# Revit family: Water_Boiler-Navien-NFB-C-Condensing-NFB-301C-02
name_source: partatom
category: Mechanical Equipment
revit_build: Autodesk Revit 2017 (Build: 20160225_1515(x64)
units: mm (PartAtom-declared; Revit-internal decimal feet)

## family parameters
Cut with Voids When Loaded = No
Host = Face
OmniClass Number = 23.65.35.11
OmniClass Title = Supply Water Heaters
Part Type = Normal
Room Calculation Point = No
Round Connector Dimension = Use Diameter
Shared = No

## types (1)
- NFB-301C
    Apparent Load = 0 VA
    Assembly Code = D3010500
    Certifications = Energy Star | AHRI | CSA | ASME | CSA Blue Star | CSA Blue Flame
    Condensate Outlet = 0.8 "
    Default Elevation = 48 "
    Depth = 22.3 "
    Description = High Efficiency Condensing Heating Boiler
    Exhaust = 3"
    Finish = Metal - Navien - Stainless Steel
    Frequency = 60 Hz
    Gas Connection Size = 1"
    Heating Capacity = 293000.0 Btu/h
    Heating Capacity Note = 20000 to 301000 BTUh
    Heating Return = 1.3 "
    Heating Supply = 1.3 "
    Height = 32.8 "
    Ignition = Electronic ignition
    Installation Type = Indoor Wall-Hung
    Intake = 3"
    Keynote = 22 33 00.A1
    Manufacturer = Navien, Inc.
    Manufacturer Fax Number = (949) 420-0430
    Model = NFB-301C
    Natural Gas Manifold Pressure = -0.06" to -0.87" WC
    Natural Gas Supply Pressure = 3.5" to 10.5" WC
    Number of Poles = 1
    Optional Heating Return = 1.3 "
    Optional Heating Supply = 1.3 "
    Phase = 1
    Power Factor = 1
    Product Documentation Link = https://www.navieninc.com
    Product Name = NFB-C Series Condensing Heating Boilers
    Product Page URL = https://www.navieninc.com
    Propane Gas Manifold Pressure = -0.01" to -0.92" WC
    Propane Gas Supply Pressure = 8.0" to 13.5" WC
    URL = https://www.navieninc.com
    Venting = Exhaust: 3" or 4" PVC, CPVC, PP and SS | 3" or 4" special gas vent type BH (Class III, A/B/C), Intake: 3" or 4" PVC, CPVC, PP and SS | 3" or 4" special gas vent type BH (Class III, A/B/C), Vent Clearance: 0" to combustibles
    Venting Type = Forced draft direct vent and non-direct vent (single pipe)
    Version = 2017 - v1.0.a
    Voltage = 120 V
    Warranty = https://www.navieninc.com
    Warranty Note = This 10/15 year limited pro-rated warranty on heat exchangers, 3/5 year limited warranty on parts, and 1 year limited-labor warranty (“Warranty”) covers defects in materials or workmanship when the Navien NFB-C Boiler (“Product”) is installed by a properly licensed plumber or contractor, and installed in strict compliance with the Installation & Operations manual procedures, subject to the terms within this Warranty document. Improper installation or use will void this Warranty. This Warranty runs from date of installation and extends to the original purchaser and subsequent owners, but only while the Product remains at the site of the original installation. This Warranty includes both a limited and pro-rated warranty as set
    Water Pressure = 12-160 psi
    Weight = 243.00 lbf
    Wi-Fi Ready = NaviLink Wi‑Fi Control: This add-on accessory enables access to control temperatures remotely, access usage data and receive diagnostic notifications via smartphone or tablet.
    Width = 25.1 "

## geometry (parser evidence)
native form markers: Sweep x4
no freeform markers — native parametric forms only
